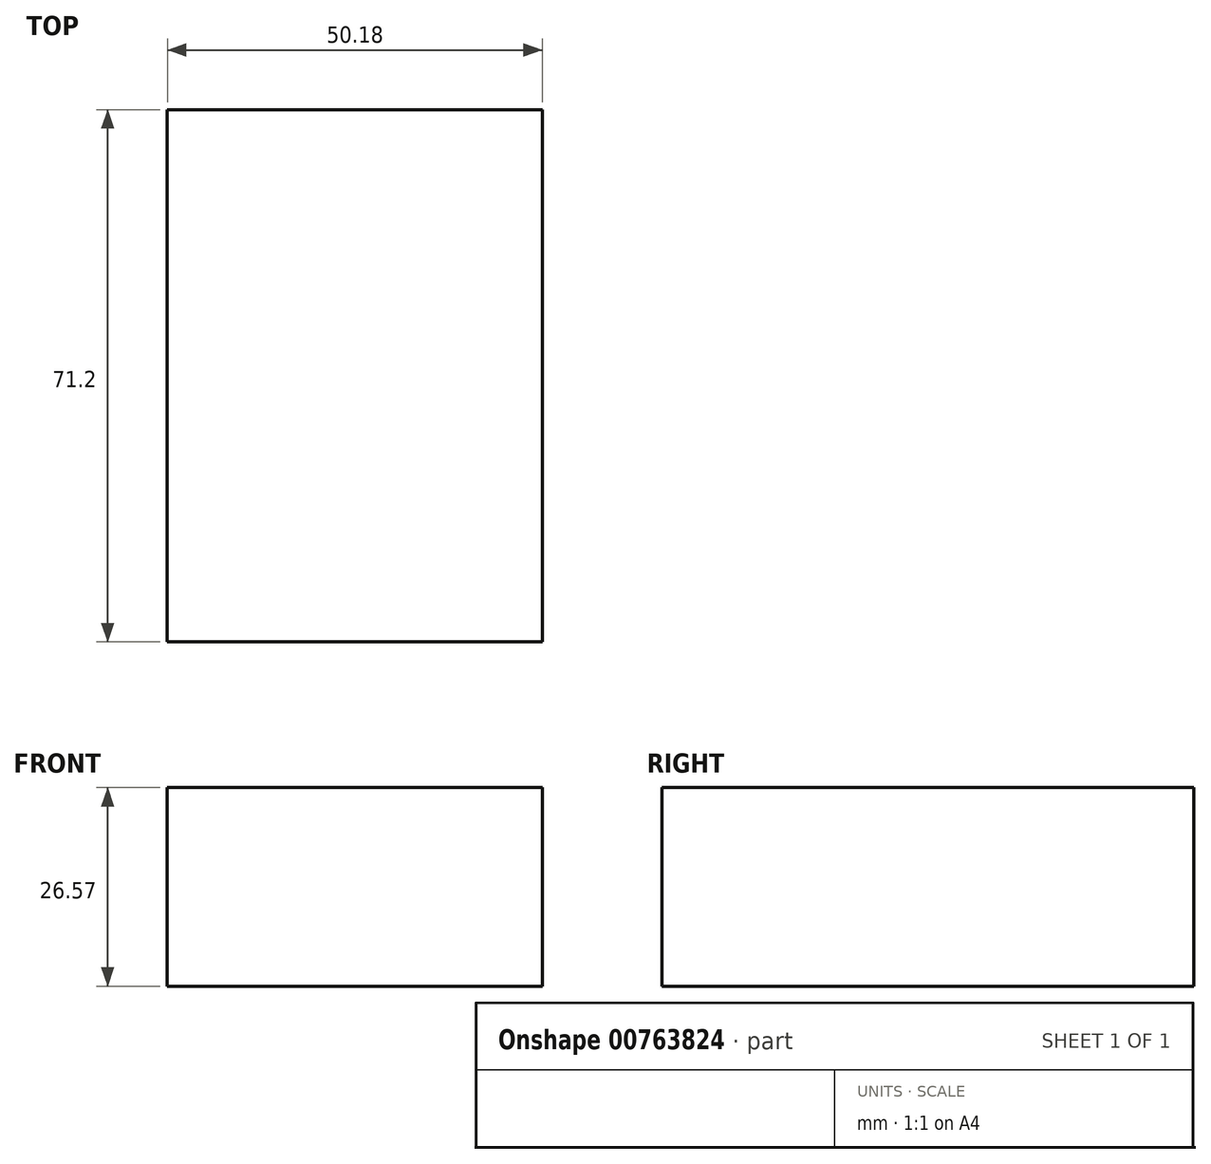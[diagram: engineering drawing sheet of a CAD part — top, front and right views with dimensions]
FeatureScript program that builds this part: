
annotation { "Feature Type Name" : "Feature", "Feature Type Description" : "" }
export const myFeature = defineFeature(function(context is Context, id is Id, definition is map)
    precondition{}
    {
        {
            var Q0;
            Q0=qCreatedBy(makeId("Front.planeOp"),FACE);
            var sketch = newSketch(context, id + "F0", { "sketchPlane" : qUnion([Q0])});
            skLineSegment(sketch, "E0.bottom", {"start": v(29.8, 19) * mm, "end": v(79.98, 19) * mm});
            skLineSegment(sketch, "E0.top", {"start": v(29.8, -7.56) * mm, "end": v(79.98, -7.56) * mm});
            skLineSegment(sketch, "E0.left", {"start": v(29.8, 19) * mm, "end": v(29.8, -7.56) * mm});
            skLineSegment(sketch, "E0.right", {"start": v(79.98, 19) * mm, "end": v(79.98, -7.56) * mm});
            skLineSegment(sketch, "E1", {"start": v(-107.64, 0) * mm, "end": v(-59.74, 43.06) * mm});
            skSolve(sketch);
        }
        {
            var Q0;
            Q0 = qSketchRegion(id + "F0", true);
            extrude(context, id + "F1", {"entities" : qUnion([Q0]), "depth" : 25 * mm, "offsetDistance" : 25 * mm});
        }
        {
            var Q0;
            Q0=makeQuery(id+"F0.imprint","IMPRINT",FACE,{"disambiguationData":[TD([[makeQuery(id+"F0.imprint","IMPRINT",EDGE,{"derivedFrom":sQuery(id+"F0.wireOp",EDGE,"E0.bottom")}),-1.0]])]});
            extrude(context, id + "F2", {"entities" : qUnion([Q0]), "operationType" : NewBodyOperationType.ADD, "depth" : 71.2 * mm, "offsetDistance" : 25 * mm});
        }
        {
            var Q0;
            Q0=sQuery(id+"F0.wireOp",EDGE,"E1");
            extrude(context, id + "F3", {"bodyType" : ToolBodyType.SURFACE, "surfaceEntities" : qUnion([Q0]), "depth" : 25 * mm, "offsetDistance" : 25 * mm});
        }
        {
            var Q0;
            Q0=sQuery(id+"F0.wireOp",EDGE,"E1");
            extrude(context, id + "F4", {"bodyType" : ToolBodyType.SURFACE, "surfaceOperationType" : NewSurfaceOperationType.ADD, "surfaceEntities" : qUnion([Q0]), "oppositeDirection" : true, "depth" : 63.1 * mm, "offsetDistance" : 25 * mm});
        }
    });
